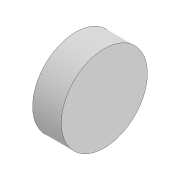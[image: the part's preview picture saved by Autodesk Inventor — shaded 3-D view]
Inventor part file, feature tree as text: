
AUTODESK INVENTOR PART (.ipt)
format: ipt  version: 2022 (Build 260153000, 153)  size: 93,184 bytes
history: native  units: mm
features: extrude x2, sketch x2
ambient origin geometry x8: Origin, YZ Plane, XZ Plane, XY Plane, X Axis, Y Axis, Z Axis, Center Point
bodies: Solid1 (feature_tree)
feature tree (4):
  extrude  "Extrusion1"  Depth=4.0mm
  extrude  "Extrusion2"  Depth=7.0mm TaperAngle=0.0deg
  sketch  "Sketch1"  dims[d1=20.0mm d2=0.0mm d5=4.0mm]
  sketch  "Sketch2"  dims[d7=6.0mm d8=7.0mm d9=0.0mm]
